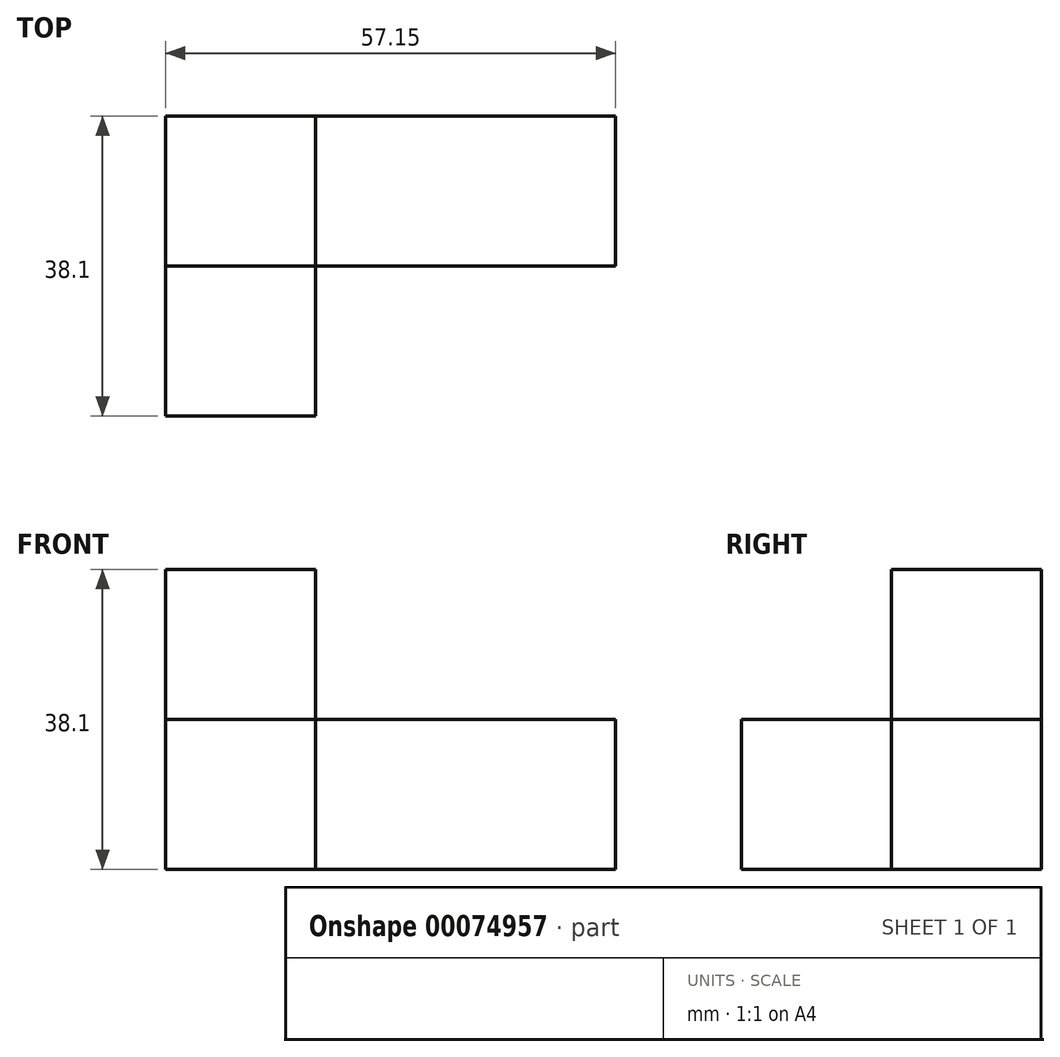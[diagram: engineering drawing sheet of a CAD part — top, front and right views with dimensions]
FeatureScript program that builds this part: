
annotation { "Feature Type Name" : "Feature", "Feature Type Description" : "" }
export const myFeature = defineFeature(function(context is Context, id is Id, definition is map)
    precondition{}
    {
        {
            var Q0;
            Q0=qCreatedBy(makeId("Front.planeOp"),FACE);
            var sketch = newSketch(context, id + "F0", { "sketchPlane" : qUnion([Q0])});
            skLineSegment(sketch, "E0.bottom", {"start": v(0, 0) * mm, "end": v(-57.15, 0) * mm});
            skLineSegment(sketch, "E0.top", {"start": v(0, 19.05) * mm, "end": v(-57.15, 19.05) * mm});
            skLineSegment(sketch, "E0.left", {"start": v(0, 0) * mm, "end": v(0, 19.05) * mm});
            skLineSegment(sketch, "E0.right", {"start": v(-57.15, 0) * mm, "end": v(-57.15, 19.05) * mm});
            skSolve(sketch);
        }
        {
            var Q0;
            Q0 = qSketchRegion(id + "F0", true);
            extrude(context, id + "F1", {"entities" : qUnion([Q0]), "depth" : 19.05 * mm});
        }
        {
            var Q0;
            Q0=makeQuery(id+"F1.opExtrude","CAP_FACE",FACE,{"disambiguationData":[OSD([sQuery(id+"F0.wireOp",EDGE,"E0.bottom"),sQuery(id+"F0.wireOp",EDGE,"E0.top"),sQuery(id+"F0.wireOp",EDGE,"E0.left"),sQuery(id+"F0.wireOp",EDGE,"E0.right")])],"isStart":false});
            var sketch = newSketch(context, id + "F2", { "sketchPlane" : qUnion([Q0])});
            skLineSegment(sketch, "E1.bottom", {"start": v(-57.15, 19.05) * mm, "end": v(-38.1, 19.05) * mm});
            skLineSegment(sketch, "E1.top", {"start": v(-57.15, 0) * mm, "end": v(-38.1, 0) * mm});
            skLineSegment(sketch, "E1.left", {"start": v(-57.15, 19.05) * mm, "end": v(-57.15, 0) * mm});
            skLineSegment(sketch, "E1.right", {"start": v(-38.1, 19.05) * mm, "end": v(-38.1, 0) * mm});
            skSolve(sketch);
        }
        {
            var Q0;
            Q0 = qSketchRegion(id + "F2", true);
            extrude(context, id + "F3", {"entities" : qUnion([Q0]), "operationType" : NewBodyOperationType.ADD, "depth" : 19.05 * mm});
        }
        {
            var Q0;
            Q0=makeQuery(id+"F3.boolean.opBoolean","MERGE",FACE,{"derivedFrom":[makeQuery(id+"F1.opExtrude","SWEPT_FACE",FACE,{"disambiguationData":[OSD([sQuery(id+"F0.wireOp",EDGE,"E0.top")])]}),makeQuery(id+"F3.opExtrude","SWEPT_FACE",FACE,{"disambiguationData":[OSD([sQuery(id+"F2.wireOp",EDGE,"E1.bottom")])]})]});
            var sketch = newSketch(context, id + "F4", { "sketchPlane" : qUnion([Q0])});
            skSolve(sketch);
        }
        {
            var Q0;
            {var subQ1=sQuery(id+"F0.wireOp",EDGE,"E0.top");Q0=makeQuery(id+"F4.imprint","IMPRINT",FACE,{"disambiguationData":[TD([[makeQuery(id+"F4.imprint","IMPRINT",EDGE,{"derivedFrom":makeQuery(id+"F1.opExtrude","CAP_EDGE",EDGE,{"disambiguationData":[OSD([subQ1])],"isStart":true})}),1.0]])]});}
            var sketch = newSketch(context, id + "F5", { "sketchPlane" : qUnion([Q0])});
            skLineSegment(sketch, "E2.bottom", {"start": v(-38.1, -19.05) * mm, "end": v(-57.15, -19.05) * mm});
            skLineSegment(sketch, "E2.top", {"start": v(-38.1, 0) * mm, "end": v(-57.15, 0) * mm});
            skLineSegment(sketch, "E2.left", {"start": v(-38.1, -19.05) * mm, "end": v(-38.1, 0) * mm});
            skLineSegment(sketch, "E2.right", {"start": v(-57.15, -19.05) * mm, "end": v(-57.15, 0) * mm});
            skSolve(sketch);
        }
        {
            var Q0;
            Q0 = qSketchRegion(id + "F5", true);
            extrude(context, id + "F6", {"entities" : qUnion([Q0]), "operationType" : NewBodyOperationType.ADD, "depth" : 19.05 * mm});
        }
    });
